# Revit family: Legrand Linkeo coffrets fixes avec panneaux latéraux amovilbles
name_source: partatom
category: Equipement spécialisé
units: mm (PartAtom-declared; Revit-internal decimal feet)

## family parameters
Basée sur le plan de construction = Non
Cote de connecteur circulaire = Utiliser le diamètre
Couper avec des vides une fois chargée = Non
Numéro OmniClass = 23.80.30.11.17
Partagée = Oui
Point de calcul de pièce = Non
Titre OmniClass = Distribution Boards and Control Panels
Toujours verticalement = Oui
Type d'élément = Normal

## types (12) — shared parameters
Avec mise à la terre = Oui
Avec parois latérales = Oui
Avec porte frontale = Oui
Avec tôle de toit = Oui
Classe d'application = Coffrets Legrand
Couleur = IDS_GRIS
Dimension modulaire = IDS_482.6_MM_19_POUCES
Démontable = Oui
Emplacement de rack = 40 mm  [stored 0.131234 ft]
Epaisseur (mm) = 1.5 mm  [stored 0.00492126 ft]
Finition de surface = Poudré
Finition du rail profilé = En forme de L
Fixation X = 400 mm  [stored 1.31234 ft]
Fonction = Coffrets fixes Linkeo Legrand
Indice de protection IK = IK08
Indice de protection IP = IP20
Largeur (mm) = 608 mm  [stored 1.99475 ft]
Lien e-catalogue = https://www.legrand.fr
Matériau = Acier
Modèle = Corps fixe
Nombre de portes = 1
Passage utile en largeur (mm) = 527 mm  [stored 1.729 ft]
RAL = 7016
Type d'aération = Passif
Type de montage = Frontal
zero-valued in all types: Elévation par défaut

## per-type parameters (varying)
| type | Capacité de charge max | EAN | Fixation Y | Hauteur (mm) | Nombre d'unités en hauteur | Passage utile en hauteur (mm) | Profondeur (mm) | Référence Legrand |
| Coffret fixe Legrand Linkeo 12U W600 D450 Flatpack 646252.rfa | 36 | 3414970968036 | 419 mm | 625 mm  [stored 2.05052 ft] | 12 | 555 mm  [stored 1.82087 ft] | 458 mm | 646252 |
| Coffret fixe Legrand Linkeo 12U W600 D600 Flatpack 646262.rfa | 36 | 3414970968098 | 419 mm | 625 mm  [stored 2.05052 ft] | 12 | 555 mm  [stored 1.82087 ft] | 608 mm  [stored 1.99475 ft] | 646262 |
| Coffret fixe Legrand Linkeo 15U W600 D450 Flatpack 646253.rfa | 45 | 3414970968043 | 552 mm  [stored 1.81102 ft] | 759 mm  [stored 2.49016 ft] | 15 | 688 mm  [stored 2.25722 ft] | 458 mm | 646253 |
| Coffret fixe Legrand Linkeo 15U W600 D600 Flatpack 646263.rfa | 45 | 3414970968104 | 552 mm  [stored 1.81102 ft] | 759 mm  [stored 2.49016 ft] | 15 | 688 mm  [stored 2.25722 ft] | 608 mm  [stored 1.99475 ft] | 646263 |
| Coffret fixe Legrand Linkeo 18U W600 D450 Flatpack 646254.rfa | 54 | 3414970968050 | 685 mm | 892 mm  [stored 2.92651 ft] | 18 | 821 mm  [stored 2.69357 ft] | 458 mm | 646254 |
| Coffret fixe Legrand Linkeo 18U W600 D600 Flatpack 646264.rfa | 54 | 3414970968111 | 685 mm | 892 mm  [stored 2.92651 ft] | 18 | 821 mm  [stored 2.69357 ft] | 608 mm  [stored 1.99475 ft] | 646264 |
| Coffret fixe Legrand Linkeo 21U W600 D450 Flatpack 646255.rfa | 63 | 3414970968067 | 819 mm  [stored 2.68701 ft] | 1025 mm  [stored 3.36286 ft] | 21 | 955 mm  [stored 3.1332 ft] | 458 mm | 646255 |
| Coffret fixe Legrand Linkeo 21U W600 D600 Flatpack 646265.rfa | 63 | 3414970968128 | 819 mm  [stored 2.68701 ft] | 1025 mm  [stored 3.36286 ft] | 21 | 955 mm  [stored 3.1332 ft] | 608 mm  [stored 1.99475 ft] | 646265 |
| Coffret fixe Legrand Linkeo 6U W600 D450 Flatpack 646250.rfa | 18 | 3414970968012 | 152 mm  [stored 0.498688 ft] | 359 mm  [stored 1.17782 ft] | 6 | 288 mm  [stored 0.944882 ft] | 458 mm | 646250 |
| Coffret fixe Legrand Linkeo 6U W600 D600 Flatpack 646260.rfa | 18 | 3414970968074 | 152 mm  [stored 0.498688 ft] | 359 mm  [stored 1.17782 ft] | 6 | 288 mm  [stored 0.944882 ft] | 608 mm  [stored 1.99475 ft] | 646260 |
| Coffret fixe Legrand Linkeo 9U W600 D450 Flatpack 646251.rfa | 27 | 3414970968029 | 286 mm | 492 mm  [stored 1.61417 ft] | 9 | 422 mm  [stored 1.38451 ft] | 458 mm | 646251 |
| Coffret fixe Legrand Linkeo 9U W600 D600 Flatpack 646261.rfa | 27 | 3414970968081 | 286 mm | 492 mm  [stored 1.61417 ft] | 9 | 422 mm  [stored 1.38451 ft] | 608 mm  [stored 1.99475 ft] | 646261 |

note: column(s) folded — value = type name in every type: Libellé BIM

note: [stored X ft] marks values corroborated as IEEE doubles in the binary element streams (Revit-internal decimal feet)
